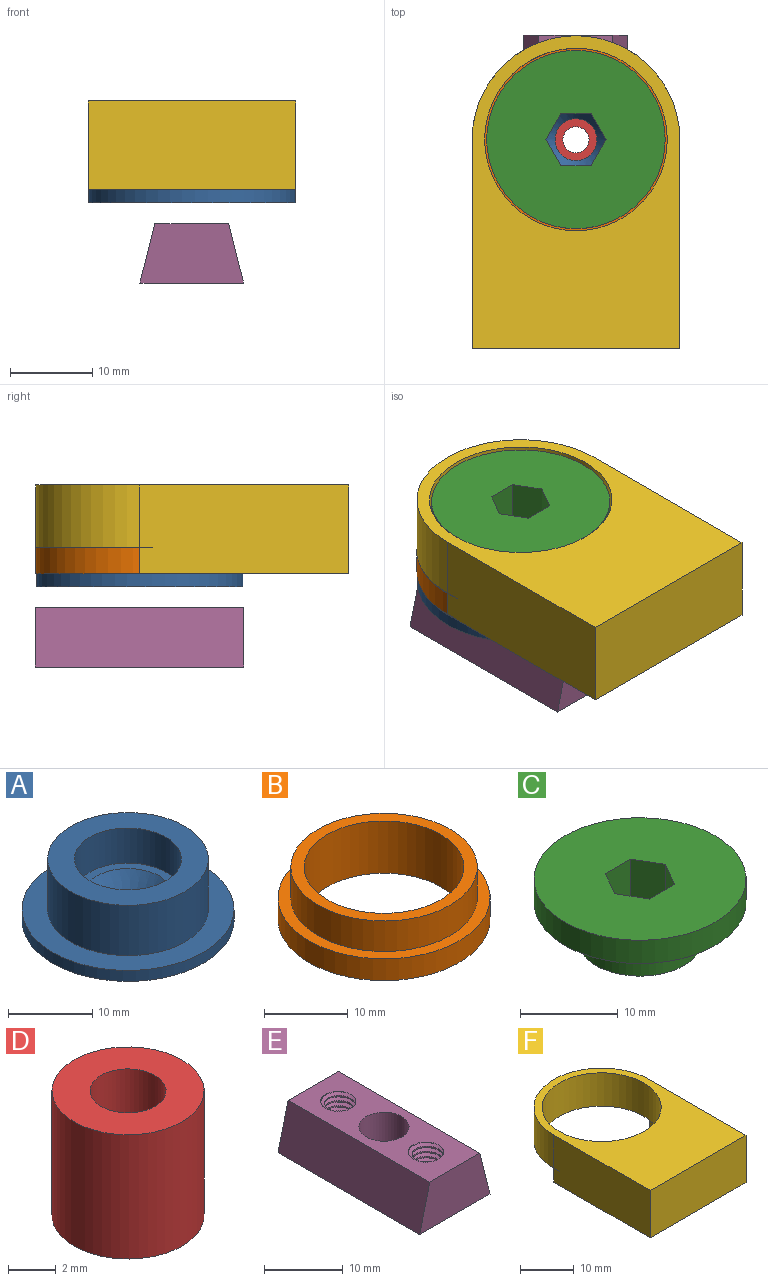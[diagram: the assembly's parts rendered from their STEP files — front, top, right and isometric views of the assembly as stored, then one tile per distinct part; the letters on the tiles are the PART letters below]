
ASSEMBLY  parts=6 mates=6
PART A: 9 faces, bbox 25.1x25.1x8.9 mm
  f0: cylinder r=9.53mm len=19.05mm, axis (0,0,1), area 437mm2, adj f6,f8
  f1: plane 12.7x12.7mm, normal (0,0,1), area 41.1mm2, adj f4,f5
  f2: plane 25.15x25.15mm, normal (0,0,-1), area 476.2mm2, adj f3,f7
  f3: cylinder r=2.55mm len=5.11mm, axis (0,0,1), area 11.9mm2, adj f2,f4
  f4: cone r=2.55mm half-angle=41deg, axis (0,0,1), area 99.3mm2, adj f1,f3
  f5: cylinder r=6.35mm len=12.7mm, axis (0,0,-1), area 202.7mm2, adj f1,f6
  f6: plane 19.05x19.05mm, normal (0,0,1), area 158.3mm2, adj f0,f5
  f7: cylinder r=12.57mm len=25.15mm, axis (0,0,-1), area 125.4mm2, adj f2,f8
  f8: plane 25.15x25.15mm, normal (0,0,1), area 211.6mm2, adj f0,f7
PART B: 6 faces, bbox 25.3x25.3x7.6 mm
  f0: cylinder r=9.53mm len=19.05mm, axis (0,0,1), area 456mm2, adj f2,f3
  f1: cylinder r=11.11mm len=22.23mm, axis (0,0,1), area 310.4mm2, adj f3,f4
  f2: plane 25.27x25.27mm, normal (0,0,-1), area 216.6mm2, adj f0,f5
  f3: plane 22.23x22.23mm, normal (0,0,1), area 102.9mm2, adj f0,f1
  f4: plane 25.27x25.27mm, normal (0,0,1), area 113.7mm2, adj f1,f5
  f5: cylinder r=12.64mm len=25.27mm, axis (0,0,1), area 252.1mm2, adj f2,f4
PART C: 11 faces, bbox 21.7x21.7x7.7 mm
  f0: plane 21.72x21.72mm, normal (0,0,1), area 335.5mm2, adj f1,f2,f3,f5,f6,f7,f8
  f1: plane 7.68x3.18mm, normal (-0.87,-0.5,0), area 28.2mm2, adj f0,f2,f6,f9
  f2: plane 7.68x3.18mm, normal (-0.87,0.5,0), area 28.2mm2, adj f0,f1,f3,f9
  f3: plane 7.68x3.67mm, normal (0,1,0), area 28.2mm2, adj f0,f2,f5,f9
  f4: plane 21.72x21.72mm, normal (0,0,-1), area 243.7mm2, adj f8,f10
  f5: plane 7.68x3.18mm, normal (0.87,0.5,0), area 28.2mm2, adj f0,f3,f7,f9
  f6: plane 7.68x3.67mm, normal (0,-1,0), area 28.2mm2, adj f0,f1,f7,f9
  f7: plane 7.68x3.18mm, normal (0.87,-0.5,0), area 28.2mm2, adj f0,f5,f6,f9
  f8: cylinder r=10.86mm len=21.72mm, axis (0,0,-1), area 199.3mm2, adj f0,f4
  f9: plane 12.7x12.7mm, normal (0,0,-1), area 91.8mm2, adj f1,f2,f3,f5,f6,f7,f10
  f10: cylinder r=6.35mm len=12.7mm, axis (0,0,1), area 190mm2, adj f4,f9
PART D: 4 faces, bbox 6.4x6.4x6.4 mm
  f0: cylinder r=1.59mm len=6.35mm, axis (0,0,-1), area 63.3mm2, adj f2,f3
  f1: cylinder r=3.17mm len=6.35mm, axis (0,0,-1), area 126.7mm2, adj f2,f3
  f2: plane 6.35x6.35mm, normal (0,0,1), area 23.8mm2, adj f0,f1
  f3: plane 6.35x6.35mm, normal (0,0,-1), area 23.8mm2, adj f0,f1
PART E: 17 faces, bbox 12.8x25.6x8 mm
  f0: plane 25.4x7.24mm, normal (0.97,0,0.24), area 189.5mm2, adj f1,f3,f4,f5
  f1: plane 25.63x9.23mm, normal (0,0,1), area 166.1mm2, adj f0,f2,f4,f5,f8,f9,f10,f11
  f2: plane 25.4x7.24mm, normal (-0.97,0,0.24), area 189.5mm2, adj f1,f3,f4,f5
  f3: plane 25.62x12.82mm, normal (0,0,-1), area 273.9mm2, adj f0,f2,f4,f5,f6,f9,f10,f11
  f4: plane 12.61x7.24mm, normal (0,-1,0), area 78.2mm2, adj f0,f1,f2,f3
  f5: plane 12.61x7.24mm, normal (0,1,0), area 78.2mm2, adj f0,f1,f2,f3
  f6: cylinder r=2.22mm len=4.45mm, axis (0,0,1), area 12.4mm2, adj f3,f7
  f7: plane 6.35x6.35mm, normal (0,0,1), area 16.2mm2, adj f6,f8
  f8: cylinder r=3.17mm len=6.35mm, axis (0,0,1), area 126.7mm2, adj f1,f7
  f9: bspline ~7.79x5.65mm, area 63.6mm2, adj f1,f3,f11,f12
  f10: bspline ~7.74x4.89mm, area 63.5mm2, adj f1,f3,f11,f12
  f11: bspline ~7.51x5.73mm, area 16.3mm2, adj f1,f3,f9,f10
  f12: cylinder r=2.02mm len=7.24mm, axis (0,0,-1), area 23.6mm2, adj f1,f3,f9,f10
  f13: bspline ~7.79x5.65mm, area 63.6mm2, adj f1,f3,f15,f16
  f14: bspline ~7.74x4.89mm, area 63.5mm2, adj f1,f3,f15,f16
  f15: bspline ~7.51x5.73mm, area 16.3mm2, adj f1,f3,f13,f14
  f16: cylinder r=2.02mm len=7.24mm, axis (0,0,-1), area 23.6mm2, adj f1,f3,f13,f14
PART F: 9 faces, bbox 25.3x38.1x10.8 mm
  f0: plane 25.27x25.27mm, normal (0,0,-1), area 113.7mm2, adj f3,f6,f8
  f1: plane 38.1x25.27mm, normal (0,0,1), area 506.4mm2, adj f2,f3,f4,f5,f6
  f2: plane 25.46x10.8mm, normal (1,0,0), area 274.9mm2, adj f1,f3,f5,f7,f8
  f3: cylinder r=12.64mm len=25.27mm, axis (0,0,-1), area 302.5mm2, adj f0,f1,f2,f4
  f4: plane 25.46x10.8mm, normal (-1,0,0), area 274.9mm2, adj f1,f3,f5,f7,f8
  f5: plane 25.27x10.8mm, normal (0,-1,0), area 272.8mm2, adj f1,f2,f4,f7
  f6: cylinder r=11.11mm len=22.23mm, axis (0,0,-1), area 532mm2, adj f0,f1
  f7: plane 25.46x25.27mm, normal (0,0,-1), area 392.7mm2, adj f2,f4,f5,f8
  f8: cylinder r=12.64mm len=25.27mm, axis (0,0,1), area 126mm2, adj f0,f2,f4,f7
PLACE A t=(0.03,-0.03,6.35)mm
PLACE B t=(0.03,-0.03,6.35)mm
PLACE C t=(0.03,-0.03,6.35)mm
PLACE D t=(0.03,-0.03,1.08)mm
PLACE E at identity fixed
PLACE F t=(0.03,-0.03,6.35)mm
MATE slider D.f1 <-> A.f7  axis (0,0,1) through (0.03,-0.03,7.43)mm
MATE fastened F.f6 <-> B.f5  axis (0,0,-1) through (0.03,-0.03,14.73)mm
MATE revolute B.f5 <-> A.f7  axis (0,0,-1) through (0.03,-0.03,11.56)mm
MATE slider A.f5 <-> C.f10  axis (0,0,-1) through (0.03,-0.03,18.86)mm
MATE fastened E.f1 <-> D.f1  axis (0,0,1) through (0.03,-0.03,7.43)mm
MATE planar B.f5 <-> C.f8  axis (0,0,1) through (0.03,-0.03,19.18)mm
